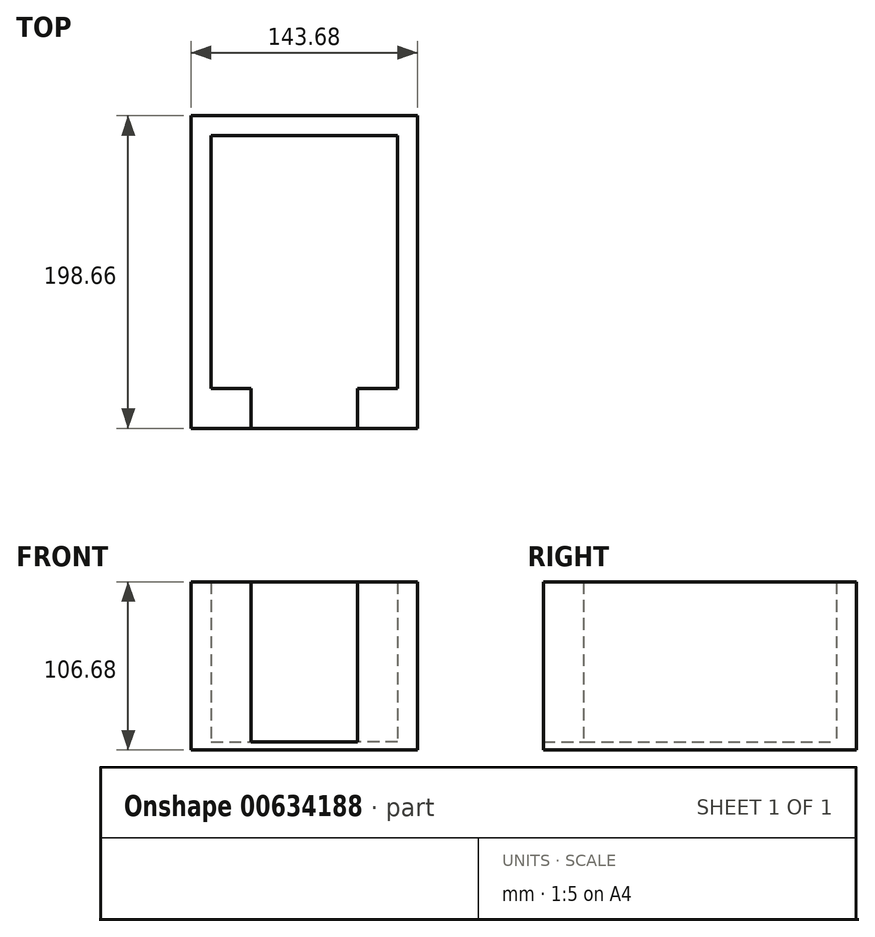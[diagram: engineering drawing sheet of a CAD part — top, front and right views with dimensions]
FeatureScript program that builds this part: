
annotation { "Feature Type Name" : "Feature", "Feature Type Description" : "" }
export const myFeature = defineFeature(function(context is Context, id is Id, definition is map)
    precondition{}
    {
        {
            var Q0;
            Q0=qCreatedBy(makeId("Top.planeOp"),FACE);
            var sketch = newSketch(context, id + "F0", { "sketchPlane" : qUnion([Q0])});
            skLineSegment(sketch, "E0.bottom", {"start": v(71.84, 99.33) * mm, "end": v(-71.84, 99.33) * mm});
            skLineSegment(sketch, "E0.top", {"start": v(71.84, -99.33) * mm, "end": v(-71.84, -99.33) * mm});
            skLineSegment(sketch, "E0.left", {"start": v(71.84, 99.33) * mm, "end": v(71.84, -99.33) * mm});
            skLineSegment(sketch, "E0.right", {"start": v(-71.84, 99.33) * mm, "end": v(-71.84, -99.33) * mm});
            skPoint(sketch, "E0.middle", {"position": v(0, 0) * mm});
            skSolve(sketch);
        }
        {
            var Q0;
            Q0=makeQuery(id+"F0.imprint","IMPRINT",FACE,{"disambiguationData":[TD([[makeQuery(id+"F0.imprint","IMPRINT",EDGE,{"derivedFrom":sQuery(id+"F0.wireOp",EDGE,"E0.bottom")}),1.0]])]});
            extrude(context, id + "F1", {"entities" : qUnion([Q0]), "depth" : 5.08 * mm, "offsetDistance" : 25.4 * mm});
        }
        {
            var Q0;
            Q0=makeQuery(id+"F1.opExtrude","CAP_FACE",FACE,{"disambiguationData":[OSD([sQuery(id+"F0.wireOp",EDGE,"E0.bottom"),sQuery(id+"F0.wireOp",EDGE,"E0.top"),sQuery(id+"F0.wireOp",EDGE,"E0.left"),sQuery(id+"F0.wireOp",EDGE,"E0.right")])],"isStart":false});
            var sketch = newSketch(context, id + "F2", { "sketchPlane" : qUnion([Q0])});
            skLineSegment(sketch, "E1.bottom", {"start": v(-71.84, 99.33) * mm, "end": v(-59.14, 99.33) * mm});
            skLineSegment(sketch, "E1.top", {"start": v(-71.84, -99.33) * mm, "end": v(-59.14, -99.33) * mm});
            skLineSegment(sketch, "E1.left", {"start": v(-71.84, 99.33) * mm, "end": v(-71.84, -99.33) * mm});
            skLineSegment(sketch, "E1.right", {"start": v(-59.14, 99.33) * mm, "end": v(-59.14, -99.33) * mm});
            skLineSegment(sketch, "E2.bottom", {"start": v(71.84, -99.33) * mm, "end": v(59.14, -99.33) * mm});
            skLineSegment(sketch, "E2.top", {"start": v(71.84, 99.33) * mm, "end": v(59.14, 99.33) * mm});
            skLineSegment(sketch, "E2.left", {"start": v(71.84, -99.33) * mm, "end": v(71.84, 99.33) * mm});
            skLineSegment(sketch, "E2.right", {"start": v(59.14, -99.33) * mm, "end": v(59.14, 99.33) * mm});
            skLineSegment(sketch, "E3.bottom", {"start": v(-59.14, 99.33) * mm, "end": v(59.14, 99.33) * mm});
            skLineSegment(sketch, "E3.top", {"start": v(-59.14, 86.63) * mm, "end": v(59.14, 86.63) * mm});
            skLineSegment(sketch, "E3.left", {"start": v(-59.14, 99.33) * mm, "end": v(-59.14, 86.63) * mm});
            skLineSegment(sketch, "E3.right", {"start": v(59.14, 99.33) * mm, "end": v(59.14, 86.63) * mm});
            skLineSegment(sketch, "E4.bottom", {"start": v(-59.14, -99.33) * mm, "end": v(-33.74, -99.33) * mm});
            skLineSegment(sketch, "E4.top", {"start": v(-59.14, -73.93) * mm, "end": v(-33.74, -73.93) * mm});
            skLineSegment(sketch, "E4.left", {"start": v(-59.14, -99.33) * mm, "end": v(-59.14, -73.93) * mm});
            skLineSegment(sketch, "E4.right", {"start": v(-33.74, -99.33) * mm, "end": v(-33.74, -73.93) * mm});
            skLineSegment(sketch, "E5.bottom", {"start": v(59.14, -99.33) * mm, "end": v(33.74, -99.33) * mm});
            skLineSegment(sketch, "E5.top", {"start": v(59.14, -73.93) * mm, "end": v(33.74, -73.93) * mm});
            skLineSegment(sketch, "E5.left", {"start": v(59.14, -99.33) * mm, "end": v(59.14, -73.93) * mm});
            skLineSegment(sketch, "E5.right", {"start": v(33.74, -99.33) * mm, "end": v(33.74, -73.93) * mm});
            skSolve(sketch);
        }
        {
            var Q0;
            Q0=makeQuery(id+"F2.imprint","IMPRINT",FACE,{"disambiguationData":[TD([[makeQuery(id+"F2.imprint","IMPRINT",EDGE,{"derivedFrom":sQuery(id+"F2.wireOp",EDGE,"E1.bottom")}),1.0]])]});
            var Q1;
            Q1=makeQuery(id+"F2.imprint","IMPRINT",FACE,{"disambiguationData":[TD([[makeQuery(id+"F2.imprint","IMPRINT",EDGE,{"derivedFrom":sQuery(id+"F2.wireOp",EDGE,"E3.bottom")}),1.0]])]});
            var Q2;
            Q2=makeQuery(id+"F2.imprint","IMPRINT",FACE,{"disambiguationData":[TD([[makeQuery(id+"F2.imprint","IMPRINT",EDGE,{"derivedFrom":sQuery(id+"F2.wireOp",EDGE,"E2.bottom")}),-1.0]])]});
            var Q3;
            Q3=makeQuery(id+"F2.imprint","IMPRINT",FACE,{"disambiguationData":[TD([[makeQuery(id+"F2.imprint","IMPRINT",EDGE,{"derivedFrom":sQuery(id+"F2.wireOp",EDGE,"E4.bottom")}),-1.0]])]});
            var Q4;
            Q4=makeQuery(id+"F2.imprint","IMPRINT",FACE,{"disambiguationData":[TD([[makeQuery(id+"F2.imprint","IMPRINT",EDGE,{"derivedFrom":sQuery(id+"F2.wireOp",EDGE,"E5.bottom")}),-1.0]])]});
            extrude(context, id + "F3", {"entities" : qUnion([Q0, Q1, Q2, Q3, Q4]), "operationType" : NewBodyOperationType.ADD, "depth" : 101.6 * mm, "offsetDistance" : 25.4 * mm});
        }
    });
